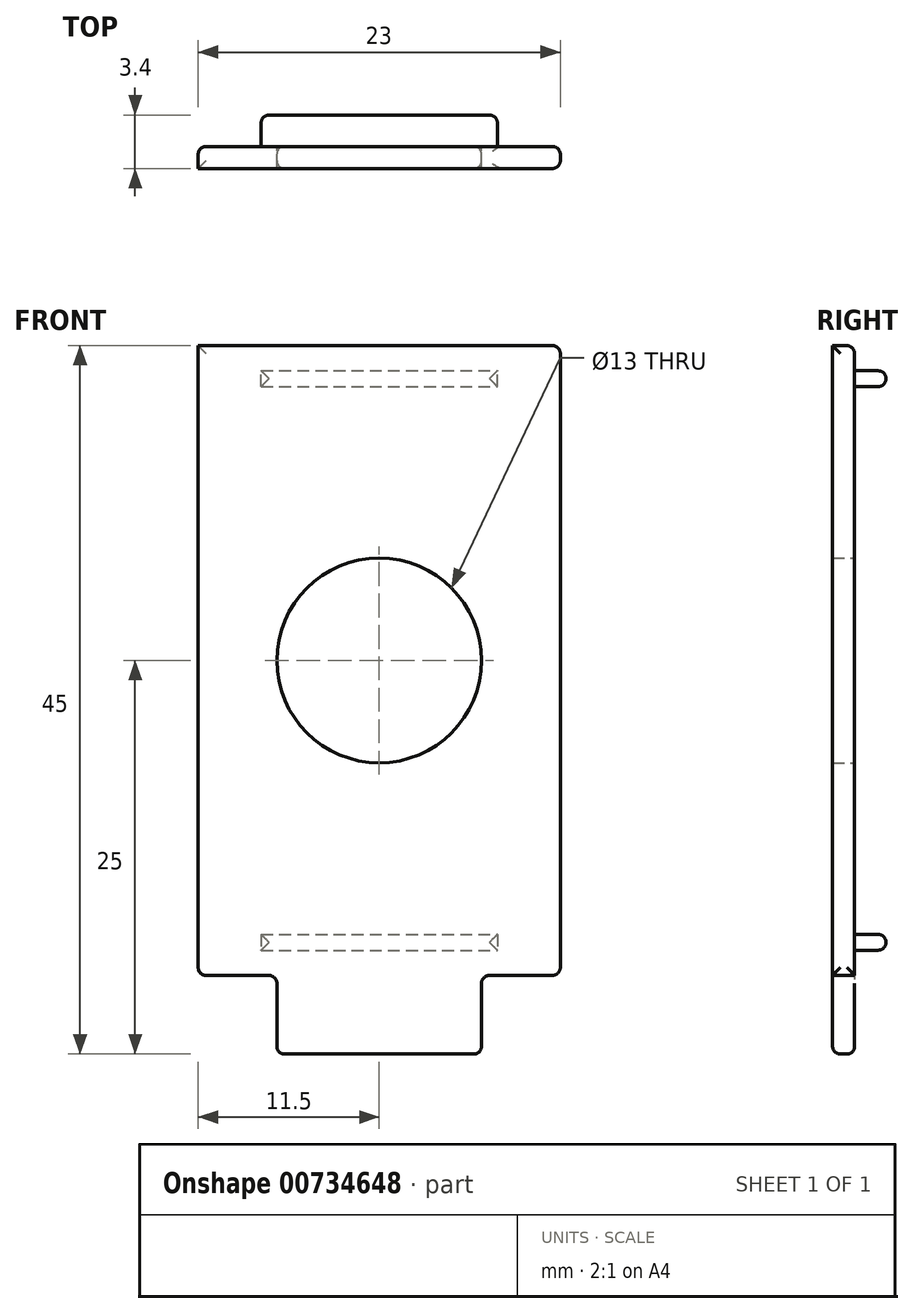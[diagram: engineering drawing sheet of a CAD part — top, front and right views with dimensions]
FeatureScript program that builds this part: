
annotation { "Feature Type Name" : "Feature", "Feature Type Description" : "" }
export const myFeature = defineFeature(function(context is Context, id is Id, definition is map)
    precondition{}
    {
        {
            var Q0;
            Q0=qCreatedBy(makeId("Front.planeOp"),FACE);
            var sketch = newSketch(context, id + "F0", { "sketchPlane" : qUnion([Q0])});
            skLineSegment(sketch, "E0.bottom", {"start": v(-11.5, 20) * mm, "end": v(11.5, 20) * mm});
            skLineSegment(sketch, "E0.top", {"start": v(-11.5, -20) * mm, "end": v(-6.5, -20) * mm});
            skLineSegment(sketch, "E0.left", {"start": v(-11.5, 20) * mm, "end": v(-11.5, -20) * mm});
            skLineSegment(sketch, "E0.right", {"start": v(11.5, 20) * mm, "end": v(11.5, -20) * mm});
            skPoint(sketch, "E0.middle", {"position": v(0, 0) * mm});
            skLineSegment(sketch, "E1.top", {"start": v(-6.5, -25) * mm, "end": v(6.5, -25) * mm});
            skLineSegment(sketch, "E1.left", {"start": v(-6.5, -20) * mm, "end": v(-6.5, -25) * mm});
            skLineSegment(sketch, "E1.right", {"start": v(6.5, -20) * mm, "end": v(6.5, -25) * mm});
            skLineSegment(sketch, "E2.trimOffspring", {"start": v(6.5, -20) * mm, "end": v(11.5, -20) * mm});
            skCircle(sketch, "E3", {"center": v(0, 0) * mm, "radius": 6.5 * mm});
            skSolve(sketch);
        }
        {
            var Q0;
            Q0 = qSketchRegion(id + "F0", true);
            extrude(context, id + "F1", {"entities" : qUnion([Q0]), "depth" : 1.4 * mm, "offsetDistance" : 25 * mm});
        }
        {
            var Q0;
            Q0=makeQuery(id+"F1.opExtrude","CAP_FACE",FACE,{"disambiguationData":[OSD([sQuery(id+"F0.wireOp",EDGE,"E0.bottom"),sQuery(id+"F0.wireOp",EDGE,"E0.top"),sQuery(id+"F0.wireOp",EDGE,"E0.left"),sQuery(id+"F0.wireOp",EDGE,"E0.right"),sQuery(id+"F0.wireOp",EDGE,"E1.top"),sQuery(id+"F0.wireOp",EDGE,"E1.left"),sQuery(id+"F0.wireOp",EDGE,"E1.right"),sQuery(id+"F0.wireOp",EDGE,"E2.trimOffspring"),sQuery(id+"F0.wireOp",EDGE,"E3")])],"isStart":true});
            var sketch = newSketch(context, id + "F2", { "sketchPlane" : qUnion([Q0])});
            skLineSegment(sketch, "E4.bottom", {"start": v(7.5, 17.4) * mm, "end": v(-7.5, 17.4) * mm});
            skLineSegment(sketch, "E4.top", {"start": v(7.5, 18.4) * mm, "end": v(-7.5, 18.4) * mm});
            skLineSegment(sketch, "E4.left", {"start": v(7.5, 17.4) * mm, "end": v(7.5, 18.4) * mm});
            skLineSegment(sketch, "E4.right", {"start": v(-7.5, 17.4) * mm, "end": v(-7.5, 18.4) * mm});
            skPoint(sketch, "E4.middle", {"position": v(0, 17.9) * mm});
            skLineSegment(sketch, "E5.MirrorCS", {"start": v(7.5, -17.4) * mm, "end": v(7.5, -18.4) * mm});
            skLineSegment(sketch, "E6.MirrorCS", {"start": v(-7.5, -17.4) * mm, "end": v(-7.5, -18.4) * mm});
            skLineSegment(sketch, "E7.MirrorCS", {"start": v(7.5, -18.4) * mm, "end": v(-7.5, -18.4) * mm});
            skLineSegment(sketch, "E8.MirrorCS", {"start": v(7.5, -17.4) * mm, "end": v(-7.5, -17.4) * mm});
            skPoint(sketch, "E9.MirrorP", {"position": v(0, -17.9) * mm});
            skSolve(sketch);
        }
        {
            var Q0;
            Q0 = qSketchRegion(id + "F2", true);
            extrude(context, id + "F3", {"entities" : qUnion([Q0]), "operationType" : NewBodyOperationType.ADD, "depth" : 2 * mm, "offsetDistance" : 25 * mm});
        }
        {
            var Q0;
            Q0=makeQuery(id+"F1.opExtrude","SWEPT_FACE",FACE,{"disambiguationData":[OSD([sQuery(id+"F0.wireOp",EDGE,"E1.top")])]});
            var Q1;
            Q1=makeQuery(id+"F1.opExtrude","SWEPT_FACE",FACE,{"disambiguationData":[OSD([sQuery(id+"F0.wireOp",EDGE,"E1.right")])]});
            var Q2;
            Q2=makeQuery(id+"F1.opExtrude","SWEPT_FACE",FACE,{"disambiguationData":[OSD([sQuery(id+"F0.wireOp",EDGE,"E0.right")])]});
            var Q3;
            Q3=makeQuery(id+"F1.opExtrude","CAP_EDGE",EDGE,{"disambiguationData":[OSD([sQuery(id+"F0.wireOp",EDGE,"E0.left")])],"isStart":true});
            var Q4;
            Q4=makeQuery(id+"F1.opExtrude","SWEPT_FACE",FACE,{"disambiguationData":[OSD([sQuery(id+"F0.wireOp",EDGE,"E1.left")])]});
            var Q5;
            Q5=makeQuery(id+"F1.opExtrude","SWEPT_FACE",FACE,{"disambiguationData":[OSD([sQuery(id+"F0.wireOp",EDGE,"E0.top")])]});
            var Q6;
            Q6=makeQuery(id+"F1.opExtrude","CAP_EDGE",EDGE,{"disambiguationData":[OSD([sQuery(id+"F0.wireOp",EDGE,"E0.bottom")])],"isStart":true});
            var Q7;
            Q7=makeQuery(id+"F3.opExtrude","CAP_FACE",FACE,{"disambiguationData":[OSD([sQuery(id+"F2.wireOp",EDGE,"E4.bottom"),sQuery(id+"F2.wireOp",EDGE,"E4.top"),sQuery(id+"F2.wireOp",EDGE,"E4.left"),sQuery(id+"F2.wireOp",EDGE,"E4.right")])],"isStart":false});
            var Q8;
            Q8=makeQuery(id+"F3.opExtrude","CAP_FACE",FACE,{"disambiguationData":[OSD([sQuery(id+"F2.wireOp",EDGE,"E5.MirrorCS"),sQuery(id+"F2.wireOp",EDGE,"E6.MirrorCS"),sQuery(id+"F2.wireOp",EDGE,"E7.MirrorCS"),sQuery(id+"F2.wireOp",EDGE,"E8.MirrorCS")])],"isStart":false});
            fillet(context, id + "F4", {"entities" : qUnion([Q0, Q1, Q2, Q3, Q4, Q5, Q6, Q7, Q8]), "tangentPropagation" : true, "radius" : 0.5 * mm, "defaultsChanged" : false, "vertexSettings" : [], "allowEdgeOverflow" : false});
        }
    });
